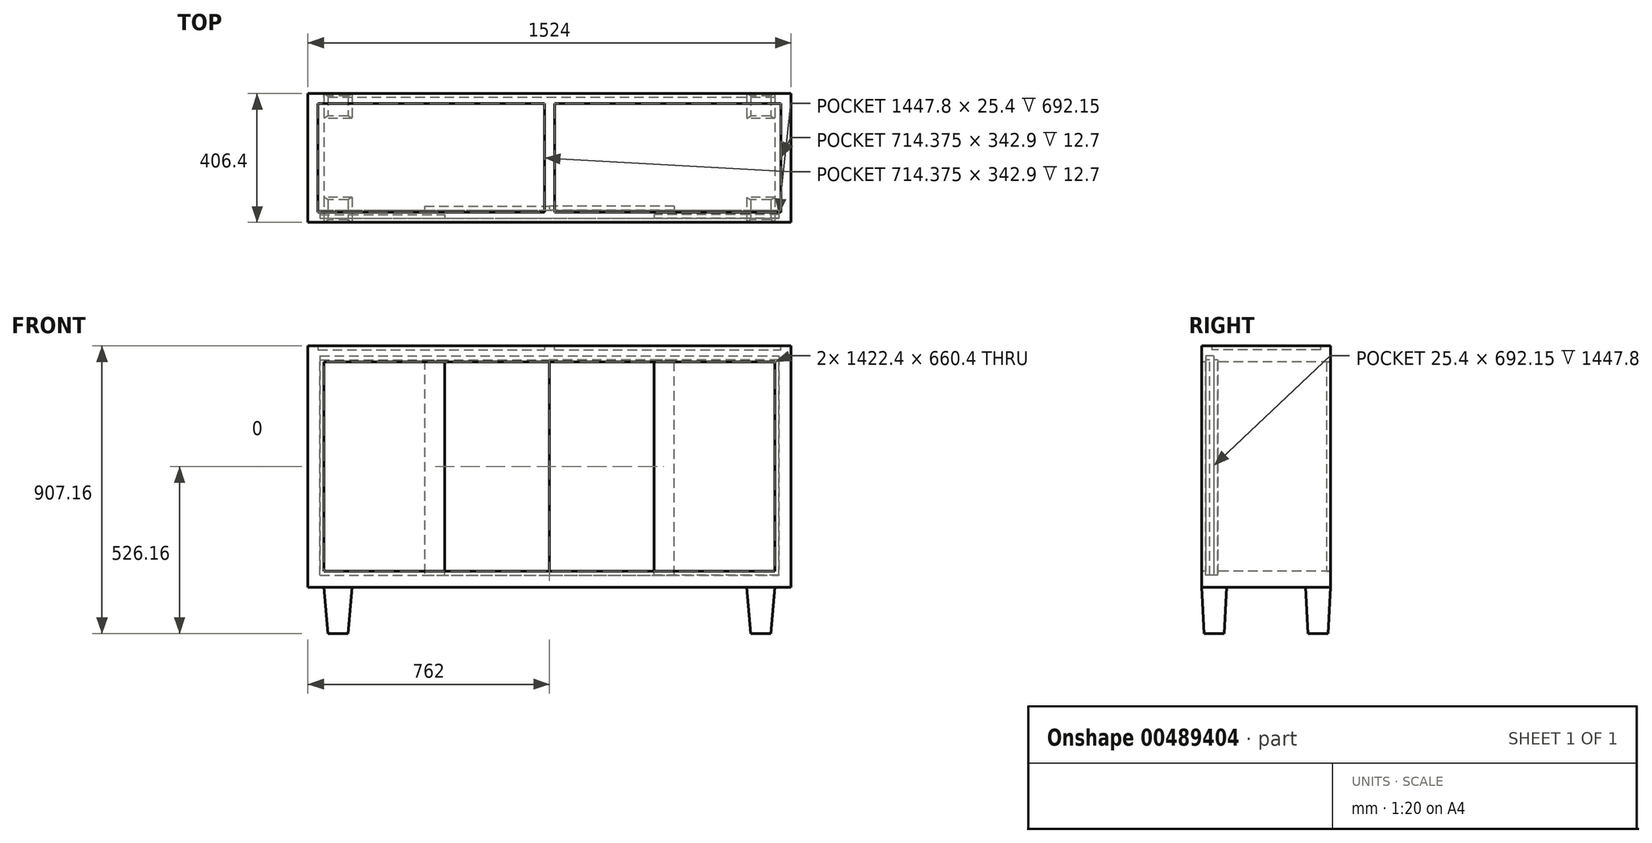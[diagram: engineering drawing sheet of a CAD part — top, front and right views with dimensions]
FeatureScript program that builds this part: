
annotation { "Feature Type Name" : "Feature", "Feature Type Description" : "" }
export const myFeature = defineFeature(function(context is Context, id is Id, definition is map)
    precondition{}
    {
        {
            var Q0;
            Q0=qCreatedBy(makeId("Front.planeOp"),FACE);
            var sketch = newSketch(context, id + "F0", { "sketchPlane" : qUnion([Q0])});
            skLineSegment(sketch, "E0.bottom", {"start": v(0, 0) * mm, "end": v(-762, 0) * mm});
            skLineSegment(sketch, "E0.top", {"start": v(0, 762) * mm, "end": v(-762, 762) * mm});
            skLineSegment(sketch, "E0.right", {"start": v(-762, 0) * mm, "end": v(-762, 762) * mm});
            skLineSegment(sketch, "E1.0", {"start": v(0, 711.2) * mm, "end": v(-711.2, 711.2) * mm});
            skLineSegment(sketch, "E2.0", {"start": v(-711.2, 50.8) * mm, "end": v(-711.2, 711.2) * mm});
            skLineSegment(sketch, "E3.0", {"start": v(0, 50.8) * mm, "end": v(-711.2, 50.8) * mm});
            skLineSegment(sketch, "E4", {"start": v(0, 762) * mm, "end": v(0, 495.3) * mm, "construction": true});
            skLineSegment(sketch, "E5", {"start": v(-711.2, 0) * mm, "end": v(-698.5, -145.16) * mm});
            skLineSegment(sketch, "E6", {"start": v(-698.5, -145.16) * mm, "end": v(-635, -145.16) * mm});
            skLineSegment(sketch, "E7", {"start": v(-635, -145.16) * mm, "end": v(-622.3, 0) * mm});
            skLineSegment(sketch, "E8.bottom", {"start": v(-711.2, 266.7) * mm, "end": v(0, 266.7) * mm});
            skLineSegment(sketch, "E8.top", {"start": v(-711.2, 288.93) * mm, "end": v(0, 288.93) * mm});
            skLineSegment(sketch, "E8.left", {"start": v(-711.2, 266.7) * mm, "end": v(-711.2, 288.93) * mm});
            skLineSegment(sketch, "E9.bottom", {"start": v(-711.2, 473.08) * mm, "end": v(0, 473.08) * mm});
            skLineSegment(sketch, "E9.top", {"start": v(-711.2, 495.3) * mm, "end": v(0, 495.3) * mm});
            skLineSegment(sketch, "E9.left", {"start": v(-711.2, 473.08) * mm, "end": v(-711.2, 495.3) * mm});
            skLineSegment(sketch, "E10.trimOffspring", {"start": v(0, 473.08) * mm, "end": v(0, 288.93) * mm, "construction": true});
            skLineSegment(sketch, "E11.trimOffspring", {"start": v(0, 266.7) * mm, "end": v(0, 0) * mm, "construction": true});
            skLineSegment(sketch, "E12.MirrorCS", {"start": v(711.2, 266.7) * mm, "end": v(711.2, 288.93) * mm});
            skLineSegment(sketch, "E13.MirrorCS", {"start": v(711.2, 473.08) * mm, "end": v(711.2, 495.3) * mm});
            skLineSegment(sketch, "E14.MirrorCS", {"start": v(698.5, -145.16) * mm, "end": v(635, -145.16) * mm});
            skLineSegment(sketch, "E15.MirrorCS", {"start": v(0, 50.8) * mm, "end": v(711.2, 50.8) * mm});
            skLineSegment(sketch, "E16.MirrorCS", {"start": v(711.2, 50.8) * mm, "end": v(711.2, 711.2) * mm});
            skLineSegment(sketch, "E17.MirrorCS", {"start": v(0, 711.2) * mm, "end": v(711.2, 711.2) * mm});
            skLineSegment(sketch, "E18.MirrorCS", {"start": v(0, 0) * mm, "end": v(762, 0) * mm});
            skLineSegment(sketch, "E19.MirrorCS", {"start": v(711.2, 473.08) * mm, "end": v(0, 473.08) * mm});
            skLineSegment(sketch, "E20.MirrorCS", {"start": v(762, 0) * mm, "end": v(762, 762) * mm});
            skLineSegment(sketch, "E21.MirrorCS", {"start": v(711.2, 495.3) * mm, "end": v(0, 495.3) * mm});
            skLineSegment(sketch, "E22.MirrorCS", {"start": v(711.2, 266.7) * mm, "end": v(0, 266.7) * mm});
            skLineSegment(sketch, "E23.MirrorCS", {"start": v(711.2, 288.93) * mm, "end": v(0, 288.93) * mm});
            skLineSegment(sketch, "E24.MirrorCS", {"start": v(635, -145.16) * mm, "end": v(622.3, 0) * mm});
            skLineSegment(sketch, "E25.MirrorCS", {"start": v(711.2, 0) * mm, "end": v(698.5, -145.16) * mm});
            skLineSegment(sketch, "E26.MirrorCS", {"start": v(0, 762) * mm, "end": v(762, 762) * mm});
            skPoint(sketch, "E27.orphan", {"position": v(-6.35, 495.3) * mm});
            skPoint(sketch, "E28.orphan", {"position": v(6.35, 495.3) * mm});
            skPoint(sketch, "E29.MirrorCS.start.orphan", {"position": v(6.35, 762) * mm});
            skPoint(sketch, "E30.0.start.orphan", {"position": v(-6.35, 762) * mm});
            skSolve(sketch);
        }
        {
            var Q0;
            Q0=makeQuery(id+"F0.imprint","IMPRINT",FACE,{"disambiguationData":[TD([[makeQuery(id+"F0.imprint","IMPRINT",EDGE,{"derivedFrom":sQuery(id+"F0.wireOp",EDGE,"E0.top")}),1.0]])]});
            var Q1;
            Q1=makeQuery(id+"F0.imprint","IMPRINT",FACE,{"disambiguationData":[TD([[makeQuery(id+"F0.imprint","IMPRINT",EDGE,{"derivedFrom":sQuery(id+"F0.wireOp",EDGE,"E14.MirrorCS")}),-1.0]])]});
            var Q2;
            {var subQ0=sQuery(id+"F0.wireOp",EDGE,"E5");Q2=makeQuery(id+"F0.imprint","IMPRINT",FACE,{"disambiguationData":[TD([[makeQuery(id+"F0.imprint","IMPRINT",EDGE,{"derivedFrom":subQ0}),1.0]])]});}
            extrude(context, id + "F1", {"entities" : qUnion([Q0, Q1, Q2]), "oppositeDirection" : true, "depth" : 406.4 * mm, "offsetDistance" : 25.4 * mm});
        }
        {
            var Q0;
            Q0=makeQuery(id+"F1.opExtrude","CAP_FACE",FACE,{"disambiguationData":[OSD([sQuery(id+"F0.wireOp",EDGE,"E0.bottom"),sQuery(id+"F0.wireOp",EDGE,"E0.top"),sQuery(id+"F0.wireOp",EDGE,"E0.right"),sQuery(id+"F0.wireOp",EDGE,"E1.0"),sQuery(id+"F0.wireOp",EDGE,"E2.0"),sQuery(id+"F0.wireOp",EDGE,"E3.0"),sQuery(id+"F0.wireOp",EDGE,"E5"),sQuery(id+"F0.wireOp",EDGE,"E6"),sQuery(id+"F0.wireOp",EDGE,"E7"),sQuery(id+"F0.wireOp",EDGE,"E8.left"),sQuery(id+"F0.wireOp",EDGE,"E9.left"),sQuery(id+"F0.wireOp",EDGE,"E14.MirrorCS"),sQuery(id+"F0.wireOp",EDGE,"E15.MirrorCS"),sQuery(id+"F0.wireOp",EDGE,"E16.MirrorCS"),sQuery(id+"F0.wireOp",EDGE,"E17.MirrorCS"),sQuery(id+"F0.wireOp",EDGE,"E18.MirrorCS"),sQuery(id+"F0.wireOp",EDGE,"E20.MirrorCS"),sQuery(id+"F0.wireOp",EDGE,"E24.MirrorCS"),sQuery(id+"F0.wireOp",EDGE,"E25.MirrorCS"),sQuery(id+"F0.wireOp",EDGE,"E26.MirrorCS")])],"isStart":false});
            cPlane(context, id + "F2", {"entities" : qUnion([Q0]), "cplaneType" : CPlaneType.OFFSET, "offset" : 0 * mm, "width" : 152.4 * mm, "height" : 152.4 * mm});
        }
        {
            var Q0;
            Q0=qCreatedBy(id+"F2.planeOp",FACE);
            var sketch = newSketch(context, id + "F3", { "sketchPlane" : qUnion([Q0])});
            skLineSegment(sketch, "E31.bottom", {"start": v(-711.2, 711.2) * mm, "end": v(711.2, 711.2) * mm});
            skLineSegment(sketch, "E31.top", {"start": v(-711.2, 50.8) * mm, "end": v(711.2, 50.8) * mm});
            skLineSegment(sketch, "E31.left", {"start": v(-711.2, 711.2) * mm, "end": v(-711.2, 50.8) * mm});
            skLineSegment(sketch, "E31.right", {"start": v(711.2, 711.2) * mm, "end": v(711.2, 50.8) * mm});
            skSolve(sketch);
        }
        {
            var Q0;
            Q0=makeQuery(id+"F3.imprint","IMPRINT",FACE,{"disambiguationData":[TD([[makeQuery(id+"F3.imprint","IMPRINT",EDGE,{"derivedFrom":sQuery(id+"F3.wireOp",EDGE,"E31.bottom")}),-1.0]])]});
            extrude(context, id + "F4", {"entities" : qUnion([Q0]), "oppositeDirection" : true, "depth" : 12.7 * mm, "offsetDistance" : 25.4 * mm});
        }
        {
            var Q0;
            Q0=makeQuery(id+"F1.opExtrude","CAP_FACE",FACE,{"disambiguationData":[OSD([sQuery(id+"F0.wireOp",EDGE,"E0.bottom"),sQuery(id+"F0.wireOp",EDGE,"E0.top"),sQuery(id+"F0.wireOp",EDGE,"E0.right"),sQuery(id+"F0.wireOp",EDGE,"E1.0"),sQuery(id+"F0.wireOp",EDGE,"E2.0"),sQuery(id+"F0.wireOp",EDGE,"E3.0"),sQuery(id+"F0.wireOp",EDGE,"E5"),sQuery(id+"F0.wireOp",EDGE,"E6"),sQuery(id+"F0.wireOp",EDGE,"E7"),sQuery(id+"F0.wireOp",EDGE,"E8.left"),sQuery(id+"F0.wireOp",EDGE,"E9.left"),sQuery(id+"F0.wireOp",EDGE,"E14.MirrorCS"),sQuery(id+"F0.wireOp",EDGE,"E15.MirrorCS"),sQuery(id+"F0.wireOp",EDGE,"E16.MirrorCS"),sQuery(id+"F0.wireOp",EDGE,"E17.MirrorCS"),sQuery(id+"F0.wireOp",EDGE,"E18.MirrorCS"),sQuery(id+"F0.wireOp",EDGE,"E20.MirrorCS"),sQuery(id+"F0.wireOp",EDGE,"E24.MirrorCS"),sQuery(id+"F0.wireOp",EDGE,"E25.MirrorCS"),sQuery(id+"F0.wireOp",EDGE,"E26.MirrorCS")])],"isStart":true});
            cPlane(context, id + "F5", {"entities" : qUnion([Q0]), "cplaneType" : CPlaneType.OFFSET, "offset" : 12.7 * mm, "oppositeDirection" : true, "width" : 152.4 * mm, "height" : 152.4 * mm});
        }
        {
            var Q0;
            Q0=qCreatedBy(id+"F5.planeOp",FACE);
            var sketch = newSketch(context, id + "F6", { "sketchPlane" : qUnion([Q0])});
            skLineSegment(sketch, "E32.bottom", {"start": v(-723.9, 730.25) * mm, "end": v(723.9, 730.25) * mm});
            skLineSegment(sketch, "E32.top", {"start": v(-723.9, 38.1) * mm, "end": v(723.9, 38.1) * mm});
            skLineSegment(sketch, "E32.left", {"start": v(-723.9, 730.25) * mm, "end": v(-723.9, 38.1) * mm});
            skLineSegment(sketch, "E32.right", {"start": v(723.9, 730.25) * mm, "end": v(723.9, 38.1) * mm});
            skSolve(sketch);
        }
        {
            var Q0;
            Q0=makeQuery(id+"F6.imprint","IMPRINT",FACE,{"disambiguationData":[TD([[makeQuery(id+"F6.imprint","IMPRINT",EDGE,{"derivedFrom":sQuery(id+"F6.wireOp",EDGE,"E32.bottom")}),-1.0]])]});
            extrude(context, id + "F7", {"entities" : qUnion([Q0]), "operationType" : NewBodyOperationType.REMOVE, "oppositeDirection" : true, "depth" : 25.4 * mm, "offsetDistance" : 25.4 * mm});
        }
        {
            var Q0;
            Q0=qCreatedBy(id+"F5.planeOp",FACE);
            var sketch = newSketch(context, id + "F8", { "sketchPlane" : qUnion([Q0])});
            skLineSegment(sketch, "E33.bottom", {"start": v(-723.9, 38.1) * mm, "end": v(-330.2, 38.1) * mm});
            skLineSegment(sketch, "E33.top", {"start": v(-723.9, 717.55) * mm, "end": v(-330.2, 717.55) * mm});
            skLineSegment(sketch, "E33.left", {"start": v(-723.9, 38.1) * mm, "end": v(-723.9, 717.55) * mm});
            skLineSegment(sketch, "E33.right", {"start": v(-330.2, 38.1) * mm, "end": v(-330.2, 717.55) * mm});
            skLineSegment(sketch, "E34.bottom", {"start": v(723.9, 38.1) * mm, "end": v(330.2, 38.1) * mm});
            skLineSegment(sketch, "E34.top", {"start": v(723.9, 717.55) * mm, "end": v(330.2, 717.55) * mm});
            skLineSegment(sketch, "E34.left", {"start": v(723.9, 38.1) * mm, "end": v(723.9, 717.55) * mm});
            skLineSegment(sketch, "E34.right", {"start": v(330.2, 38.1) * mm, "end": v(330.2, 717.55) * mm});
            skSolve(sketch);
        }
        {
            var Q0;
            Q0=makeQuery(id+"F8.imprint","IMPRINT",FACE,{"disambiguationData":[TD([[makeQuery(id+"F8.imprint","IMPRINT",EDGE,{"derivedFrom":sQuery(id+"F8.wireOp",EDGE,"E33.bottom")}),1.0]])]});
            var Q1;
            Q1=makeQuery(id+"F8.imprint","IMPRINT",FACE,{"disambiguationData":[TD([[makeQuery(id+"F8.imprint","IMPRINT",EDGE,{"derivedFrom":sQuery(id+"F8.wireOp",EDGE,"E34.bottom")}),-1.0]])]});
            extrude(context, id + "F9", {"entities" : qUnion([Q0, Q1]), "oppositeDirection" : true, "depth" : 12.2 * mm, "offsetDistance" : 25.4 * mm});
        }
        {
            var Q0;
            Q0=makeQuery(id+"F7.boolean.opBoolean","COPY",FACE,{"derivedFrom":makeQuery(id+"F7.opExtrude","CAP_FACE",FACE,{"disambiguationData":[OSD([sQuery(id+"F6.wireOp",EDGE,"E32.bottom"),sQuery(id+"F6.wireOp",EDGE,"E32.top"),sQuery(id+"F6.wireOp",EDGE,"E32.left"),sQuery(id+"F6.wireOp",EDGE,"E32.right")])],"isStart":false})});
            var sketch = newSketch(context, id + "F10", { "sketchPlane" : qUnion([Q0])});
            skLineSegment(sketch, "E35.bottom", {"start": v(-393.79, 717.55) * mm, "end": v(-0.09, 717.55) * mm});
            skLineSegment(sketch, "E35.top", {"start": v(-393.79, 38.1) * mm, "end": v(-0.09, 38.1) * mm});
            skLineSegment(sketch, "E35.left", {"start": v(-393.79, 717.55) * mm, "end": v(-393.79, 38.1) * mm});
            skLineSegment(sketch, "E35.right", {"start": v(-0.09, 717.55) * mm, "end": v(-0.09, 38.1) * mm});
            skLineSegment(sketch, "E36.bottom", {"start": v(393.61, 38.1) * mm, "end": v(-0.09, 38.1) * mm});
            skLineSegment(sketch, "E36.top", {"start": v(393.61, 717.55) * mm, "end": v(-0.09, 717.55) * mm});
            skLineSegment(sketch, "E36.left", {"start": v(393.61, 38.1) * mm, "end": v(393.61, 717.55) * mm});
            skLineSegment(sketch, "E36.right", {"start": v(-0.09, 38.1) * mm, "end": v(-0.09, 717.55) * mm});
            skSolve(sketch);
        }
        {
            var Q0;
            {var subQ0=sQuery(id+"F10.wireOp",EDGE,"E35.top");Q0=makeQuery(id+"F10.imprint","IMPRINT",FACE,{"disambiguationData":[TD([[makeQuery(id+"F10.imprint","IMPRINT",EDGE,{"derivedFrom":subQ0}),1.0]])]});}
            var Q1;
            {var subQ0=sQuery(id+"F10.wireOp",EDGE,"E35.left");var subQ1=makeQuery(id+"F7.opExtrude","CAP_FACE",FACE,{"disambiguationData":[OSD([sQuery(id+"F6.wireOp",EDGE,"E32.bottom"),sQuery(id+"F6.wireOp",EDGE,"E32.top"),sQuery(id+"F6.wireOp",EDGE,"E32.left"),sQuery(id+"F6.wireOp",EDGE,"E32.right")])],"isStart":false});var subQ2=makeQuery(id+"F7.boolean.opBoolean","INTERSECT",EDGE,{"derivedFrom":[makeQuery(id+"F1.opExtrude","SWEPT_FACE",FACE,{"disambiguationData":[OSD([sQuery(id+"F0.wireOp",EDGE,"E1.0"),sQuery(id+"F0.wireOp",EDGE,"E17.MirrorCS")])]}),subQ1]});var subQ3=makeQuery(id+"F10.imprint","INTERSECT",VERTEX,{"derivedFrom":[subQ2,subQ0]});Q1=makeQuery(id+"F10.imprint","IMPRINT",FACE,{"disambiguationData":[TD([[makeQuery(id+"F10.imprint","IMPRINT",EDGE,{"disambiguationData":[TD([[subQ3,-1.0]])],"derivedFrom":subQ0}),1.0]])]});}
            var Q2;
            {var subQ0=sQuery(id+"F10.wireOp",EDGE,"E35.bottom");Q2=makeQuery(id+"F10.imprint","IMPRINT",FACE,{"disambiguationData":[TD([[makeQuery(id+"F10.imprint","IMPRINT",EDGE,{"derivedFrom":subQ0}),-1.0]])]});}
            extrude(context, id + "F11", {"entities" : qUnion([Q0, Q1, Q2]), "oppositeDirection" : true, "depth" : 12.45 * mm, "offsetDistance" : 25.4 * mm});
        }
        {
            var Q0;
            {var subQ0=sQuery(id+"F10.wireOp",EDGE,"E36.left");var subQ1=makeQuery(id+"F7.opExtrude","CAP_FACE",FACE,{"disambiguationData":[OSD([sQuery(id+"F6.wireOp",EDGE,"E32.bottom"),sQuery(id+"F6.wireOp",EDGE,"E32.top"),sQuery(id+"F6.wireOp",EDGE,"E32.left"),sQuery(id+"F6.wireOp",EDGE,"E32.right")])],"isStart":false});var subQ2=makeQuery(id+"F7.boolean.opBoolean","INTERSECT",EDGE,{"derivedFrom":[makeQuery(id+"F1.opExtrude","SWEPT_FACE",FACE,{"disambiguationData":[OSD([sQuery(id+"F0.wireOp",EDGE,"E3.0"),sQuery(id+"F0.wireOp",EDGE,"E15.MirrorCS")])]}),subQ1]});var subQ3=makeQuery(id+"F10.imprint","INTERSECT",VERTEX,{"derivedFrom":[subQ2,subQ0]});Q0=makeQuery(id+"F10.imprint","IMPRINT",FACE,{"disambiguationData":[TD([[makeQuery(id+"F10.imprint","IMPRINT",EDGE,{"disambiguationData":[TD([[subQ3,-1.0]])],"derivedFrom":subQ0}),1.0]])]});}
            var Q1;
            {var subQ0=sQuery(id+"F10.wireOp",EDGE,"E36.top");Q1=makeQuery(id+"F10.imprint","IMPRINT",FACE,{"disambiguationData":[TD([[makeQuery(id+"F10.imprint","IMPRINT",EDGE,{"derivedFrom":subQ0}),1.0]])]});}
            var Q2;
            {var subQ0=sQuery(id+"F10.wireOp",EDGE,"E36.bottom");Q2=makeQuery(id+"F10.imprint","IMPRINT",FACE,{"disambiguationData":[TD([[makeQuery(id+"F10.imprint","IMPRINT",EDGE,{"derivedFrom":subQ0}),1.0]])]});}
            extrude(context, id + "F12", {"entities" : qUnion([Q0, Q1, Q2]), "oppositeDirection" : true, "depth" : 12.7 * mm, "offsetDistance" : 25.4 * mm});
        }
        {
            var Q0;
            Q0=makeQuery(id+"F1.opExtrude","SWEPT_FACE",FACE,{"disambiguationData":[OSD([sQuery(id+"F0.wireOp",EDGE,"E0.right")])]});
            var sketch = newSketch(context, id + "F13", { "sketchPlane" : qUnion([Q0])});
            skLineSegment(sketch, "E37", {"start": v(0, 0) * mm, "end": v(-7.6, -145.16) * mm});
            skLineSegment(sketch, "E38", {"start": v(-7.6, -145.16) * mm, "end": v(-71.1, -145.16) * mm});
            skLineSegment(sketch, "E39", {"start": v(-71.1, -145.16) * mm, "end": v(-78.72, 0) * mm});
            skLineSegment(sketch, "E40", {"start": v(-406.4, 0) * mm, "end": v(-398.8, -145.16) * mm});
            skLineSegment(sketch, "E41", {"start": v(-398.8, -145.16) * mm, "end": v(-335.3, -145.16) * mm});
            skLineSegment(sketch, "E42", {"start": v(-335.3, -145.16) * mm, "end": v(-327.68, 0) * mm});
            skLineSegment(sketch, "E43", {"start": v(-203.2, 0) * mm, "end": v(-203.2, -187.84) * mm, "construction": true});
            skLineSegment(sketch, "E44", {"start": v(-406.4, 0) * mm, "end": v(-529.31, 0) * mm});
            skLineSegment(sketch, "E45", {"start": v(-529.31, 0) * mm, "end": v(-529.31, -225.64) * mm});
            skLineSegment(sketch, "E46", {"start": v(-529.31, -225.64) * mm, "end": v(113.12, -225.64) * mm});
            skLineSegment(sketch, "E47", {"start": v(113.12, -225.64) * mm, "end": v(113.12, 0) * mm});
            skLineSegment(sketch, "E48", {"start": v(113.12, 0) * mm, "end": v(0, 0) * mm});
            skLineSegment(sketch, "E49", {"start": v(-327.68, 0) * mm, "end": v(-78.72, 0) * mm});
            skSolve(sketch);
        }
        {
            var Q0;
            Q0=makeQuery(id+"F13.imprint","IMPRINT",FACE,{"disambiguationData":[TD([[makeQuery(id+"F13.imprint","IMPRINT",EDGE,{"derivedFrom":sQuery(id+"F13.wireOp",EDGE,"E37")}),1.0]])]});
            extrude(context, id + "F14", {"entities" : qUnion([Q0]), "operationType" : NewBodyOperationType.REMOVE, "endBound" : BoundingType.THROUGH_ALL, "oppositeDirection" : true, "depth" : 25.4 * mm, "offsetDistance" : 25.4 * mm});
        }
        {
            var Q0;
            Q0=makeQuery(id+"F1.opExtrude","SWEPT_FACE",FACE,{"disambiguationData":[OSD([sQuery(id+"F0.wireOp",EDGE,"E0.top"),sQuery(id+"F0.wireOp",EDGE,"E26.MirrorCS")])]});
            var sketch = newSketch(context, id + "F15", { "sketchPlane" : qUnion([Q0])});
            skLineSegment(sketch, "E50.bottom", {"start": v(-730.25, 374.65) * mm, "end": v(-15.87, 374.65) * mm});
            skLineSegment(sketch, "E50.top", {"start": v(-730.25, 31.75) * mm, "end": v(-15.87, 31.75) * mm});
            skLineSegment(sketch, "E50.left", {"start": v(-730.25, 374.65) * mm, "end": v(-730.25, 31.75) * mm});
            skLineSegment(sketch, "E50.right", {"start": v(730.25, 374.65) * mm, "end": v(730.25, 31.75) * mm});
            skLineSegment(sketch, "E51.0", {"start": v(-15.88, 374.65) * mm, "end": v(-15.87, 31.75) * mm});
            skLineSegment(sketch, "E52.0", {"start": v(15.87, 374.65) * mm, "end": v(15.88, 31.75) * mm});
            skPoint(sketch, "E53.end.orphan", {"position": v(0, 31.75) * mm});
            skPoint(sketch, "E53.start.orphan", {"position": v(0, 374.65) * mm});
            skLineSegment(sketch, "E54.trimOffspring", {"start": v(15.87, 374.65) * mm, "end": v(730.25, 374.65) * mm});
            skLineSegment(sketch, "E55.trimOffspring", {"start": v(15.87, 31.75) * mm, "end": v(730.25, 31.75) * mm});
            skSolve(sketch);
        }
        {
            var Q0;
            Q0=makeQuery(id+"F15.imprint","IMPRINT",FACE,{"disambiguationData":[TD([[makeQuery(id+"F15.imprint","IMPRINT",EDGE,{"derivedFrom":sQuery(id+"F15.wireOp",EDGE,"E50.bottom")}),-1.0]])]});
            var Q1;
            Q1=makeQuery(id+"F15.imprint","IMPRINT",FACE,{"disambiguationData":[TD([[makeQuery(id+"F15.imprint","IMPRINT",EDGE,{"derivedFrom":sQuery(id+"F15.wireOp",EDGE,"E50.right")}),-1.0]])]});
            extrude(context, id + "F16", {"entities" : qUnion([Q0, Q1]), "operationType" : NewBodyOperationType.REMOVE, "oppositeDirection" : true, "depth" : 12.7 * mm, "offsetDistance" : 25.4 * mm});
        }
        {
            var Q0;
            Q0=makeQuery(id+"F16.boolean.opBoolean","COPY",FACE,{"derivedFrom":makeQuery(id+"F16.opExtrude","CAP_FACE",FACE,{"disambiguationData":[OSD([sQuery(id+"F15.wireOp",EDGE,"E50.bottom"),sQuery(id+"F15.wireOp",EDGE,"E50.top"),sQuery(id+"F15.wireOp",EDGE,"E50.left"),sQuery(id+"F15.wireOp",EDGE,"E51.0")])],"isStart":false})});
            var Q1;
            Q1=makeQuery(id+"F16.boolean.opBoolean","COPY",FACE,{"derivedFrom":makeQuery(id+"F16.opExtrude","CAP_FACE",FACE,{"disambiguationData":[OSD([sQuery(id+"F15.wireOp",EDGE,"E50.right"),sQuery(id+"F15.wireOp",EDGE,"E52.0"),sQuery(id+"F15.wireOp",EDGE,"E54.trimOffspring"),sQuery(id+"F15.wireOp",EDGE,"E55.trimOffspring")])],"isStart":false})});
            extrude(context, id + "F17", {"entities" : qUnion([Q0, Q1]), "depth" : 12.7 * mm, "offsetDistance" : 25.4 * mm});
        }
    });
